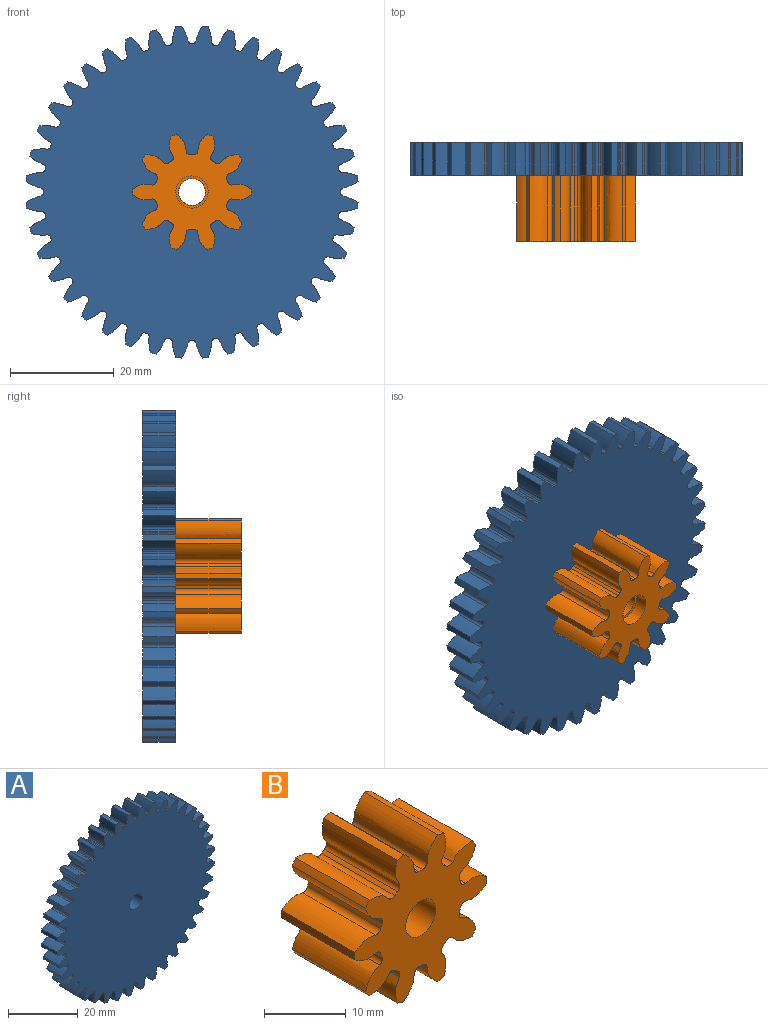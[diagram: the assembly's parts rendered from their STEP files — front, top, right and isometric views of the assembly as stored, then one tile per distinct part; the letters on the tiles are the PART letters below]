
ASSEMBLY  parts=2 mates=1
PART A: 245 faces, bbox 63.9x6.4x63.9 mm
  f0: cylinder r=2.59mm len=5.18mm, axis (0,-1,0), area 62.7mm2, adj f40,f243
  f1: cylinder r=32mm len=6.35mm, axis (0,1,0), area 7.4mm2, adj f40,f42,f148,f240
  f2: cylinder r=32mm len=6.35mm, axis (0,1,0), area 7.4mm2, adj f40,f42,f235,f238
  f3: cylinder r=32mm len=6.35mm, axis (0,1,0), area 7.4mm2, adj f40,f42,f230,f233
  f4: cylinder r=32mm len=6.35mm, axis (0,1,0), area 7.4mm2, adj f40,f42,f225,f228
  f5: cylinder r=32mm len=6.35mm, axis (0,1,0), area 7.4mm2, adj f40,f42,f220,f223
  f6: cylinder r=32mm len=6.35mm, axis (0,1,0), area 7.4mm2, adj f40,f42,f215,f218
  f7: cylinder r=32mm len=6.35mm, axis (0,1,0), area 7.4mm2, adj f40,f42,f210,f213
  f8: cylinder r=32mm len=6.35mm, axis (0,1,0), area 7.4mm2, adj f40,f42,f205,f208
  f9: cylinder r=32mm len=6.35mm, axis (0,1,0), area 7.4mm2, adj f40,f42,f193,f200
  f10: cylinder r=32mm len=6.35mm, axis (0,1,0), area 7.4mm2, adj f40,f42,f195,f203
  f11: cylinder r=32mm len=6.35mm, axis (0,1,0), area 7.4mm2, adj f40,f42,f190,f198
  f12: cylinder r=32mm len=6.35mm, axis (0,1,0), area 7.4mm2, adj f40,f42,f185,f188
  f13: cylinder r=32mm len=6.35mm, axis (0,1,0), area 7.4mm2, adj f40,f42,f180,f183
  f14: cylinder r=32mm len=6.35mm, axis (0,1,0), area 7.4mm2, adj f40,f42,f175,f178
  f15: cylinder r=32mm len=6.35mm, axis (0,1,0), area 7.4mm2, adj f40,f42,f170,f173
  f16: cylinder r=32mm len=6.35mm, axis (0,1,0), area 7.4mm2, adj f40,f42,f165,f168
  f17: cylinder r=32mm len=6.35mm, axis (0,1,0), area 7.4mm2, adj f40,f42,f138,f160
  f18: cylinder r=32mm len=6.35mm, axis (0,1,0), area 7.4mm2, adj f40,f42,f155,f158
  f19: cylinder r=32mm len=6.35mm, axis (0,1,0), area 7.4mm2, adj f40,f42,f143,f150
  f20: cylinder r=32mm len=6.35mm, axis (0,1,0), area 7.4mm2, adj f40,f42,f145,f153
  f21: cylinder r=32mm len=6.35mm, axis (0,1,0), area 7.4mm2, adj f40,f42,f133,f140
  f22: cylinder r=32mm len=6.35mm, axis (0,1,0), area 7.4mm2, adj f40,f42,f128,f135
  f23: cylinder r=32mm len=6.35mm, axis (0,1,0), area 7.4mm2, adj f40,f42,f123,f130
  f24: cylinder r=32mm len=6.35mm, axis (0,1,0), area 7.4mm2, adj f40,f42,f83,f125
  f25: cylinder r=32mm len=6.35mm, axis (0,1,0), area 7.4mm2, adj f40,f42,f43,f120
  f26: cylinder r=32mm len=6.35mm, axis (0,1,0), area 7.4mm2, adj f40,f42,f115,f118
  f27: cylinder r=32mm len=6.35mm, axis (0,1,0), area 7.4mm2, adj f40,f42,f110,f113
  f28: cylinder r=32mm len=6.35mm, axis (0,1,0), area 7.4mm2, adj f40,f42,f105,f108
  f29: cylinder r=32mm len=6.35mm, axis (0,1,0), area 7.4mm2, adj f40,f42,f93,f100
  f30: cylinder r=32mm len=6.35mm, axis (0,1,0), area 7.4mm2, adj f40,f42,f95,f103
  f31: cylinder r=32mm len=6.35mm, axis (0,1,0), area 7.4mm2, adj f40,f42,f90,f98
  f32: cylinder r=32mm len=6.35mm, axis (0,1,0), area 7.4mm2, adj f40,f42,f85,f88
  f33: cylinder r=32mm len=6.35mm, axis (0,1,0), area 7.4mm2, adj f40,f42,f68,f80
  f34: cylinder r=32mm len=6.35mm, axis (0,1,0), area 7.4mm2, adj f40,f42,f75,f78
  f35: cylinder r=32mm len=6.35mm, axis (0,1,0), area 7.4mm2, adj f40,f42,f63,f70
  f36: cylinder r=32mm len=6.35mm, axis (0,1,0), area 7.4mm2, adj f40,f42,f65,f163
  f37: cylinder r=32mm len=6.35mm, axis (0,1,0), area 7.4mm2, adj f40,f42,f60,f73
  f38: cylinder r=32mm len=6.35mm, axis (0,1,0), area 7.4mm2, adj f40,f42,f55,f58
  f39: cylinder r=32mm len=6.35mm, axis (0,1,0), area 7.4mm2, adj f40,f42,f50,f53
  f40: plane 63.89x63.89mm, normal (0,-1,0), area 2875.7mm2, adj f0,f1,f2,f3,f4,f5,f6,f7
  f41: cylinder r=32mm len=6.35mm, axis (0,1,0), area 7.4mm2, adj f40,f42,f45,f48
  f42: plane 63.89x63.89mm, normal (0,1,0), area 2866.6mm2, adj f1,f2,f3,f4,f5,f6,f7,f8
  f43: extruded ~6.35x2.93mm, area 20.2mm2, adj f25,f40,f42,f46
  f44: cylinder r=28.57mm len=6.35mm, axis (0,1,0), area 2.7mm2, adj f40,f42,f46,f47
  f45: extruded ~6.35x2.93mm, area 20.2mm2, adj f40,f41,f42,f47
  f46: cylinder r=0.54mm len=6.35mm, axis (0,1,0), area 4.8mm2, adj f40,f42,f43,f44
  f47: cylinder r=0.54mm len=6.35mm, axis (0,1,0), area 4.8mm2, adj f40,f42,f44,f45
  f48: extruded ~6.35x3.08mm, area 20.2mm2, adj f40,f41,f42,f51
  f49: cylinder r=28.57mm len=6.35mm, axis (0,1,0), area 2.7mm2, adj f40,f42,f51,f52
  f50: extruded ~6.35x2.71mm, area 20.2mm2, adj f39,f40,f42,f52
  f51: cylinder r=0.54mm len=6.35mm, axis (0,1,0), area 4.8mm2, adj f40,f42,f48,f49
  f52: cylinder r=0.54mm len=6.35mm, axis (0,1,0), area 4.8mm2, adj f40,f42,f49,f50
  f53: extruded ~6.35x3.16mm, area 20.2mm2, adj f39,f40,f42,f56
  f54: cylinder r=28.57mm len=6.35mm, axis (0,1,0), area 2.7mm2, adj f40,f42,f56,f57
  f55: extruded ~6.35x2.42mm, area 20.2mm2, adj f38,f40,f42,f57
  f56: cylinder r=0.54mm len=6.35mm, axis (0,1,0), area 4.8mm2, adj f40,f42,f53,f54
  f57: cylinder r=0.54mm len=6.35mm, axis (0,1,0), area 4.8mm2, adj f40,f42,f54,f55
  f58: extruded ~6.35x3.15mm, area 20.2mm2, adj f38,f40,f42,f61
  f59: cylinder r=28.57mm len=6.35mm, axis (0,1,0), area 2.7mm2, adj f40,f42,f61,f62
  f60: extruded ~6.35x2.39mm, area 20.2mm2, adj f37,f40,f42,f62
  f61: cylinder r=0.54mm len=6.35mm, axis (0,1,0), area 4.8mm2, adj f40,f42,f58,f59
  f62: cylinder r=0.54mm len=6.35mm, axis (0,1,0), area 4.8mm2, adj f40,f42,f59,f60
  f63: extruded ~6.35x2.39mm, area 20.2mm2, adj f35,f40,f42,f66
  f64: cylinder r=28.57mm len=6.35mm, axis (0,1,0), area 2.7mm2, adj f40,f42,f66,f67
  f65: extruded ~6.35x3.15mm, area 20.2mm2, adj f36,f40,f42,f67
  f66: cylinder r=0.54mm len=6.35mm, axis (0,1,0), area 4.8mm2, adj f40,f42,f63,f64
  f67: cylinder r=0.54mm len=6.35mm, axis (0,1,0), area 4.8mm2, adj f40,f42,f64,f65
  f68: extruded ~6.35x2.68mm, area 20.2mm2, adj f33,f40,f42,f71
  f69: cylinder r=28.57mm len=6.35mm, axis (0,1,0), area 2.7mm2, adj f40,f42,f71,f72
  f70: extruded ~6.35x3.07mm, area 20.2mm2, adj f35,f40,f42,f72
  f71: cylinder r=0.54mm len=6.35mm, axis (0,1,0), area 4.8mm2, adj f40,f42,f68,f69
  f72: cylinder r=0.54mm len=6.35mm, axis (0,1,0), area 4.8mm2, adj f40,f42,f69,f70
  f73: extruded ~6.35x3.07mm, area 20.2mm2, adj f37,f40,f42,f76
  f74: cylinder r=28.57mm len=6.35mm, axis (0,1,0), area 2.7mm2, adj f40,f42,f76,f77
  f75: extruded ~6.35x2.68mm, area 20.2mm2, adj f34,f40,f42,f77
  f76: cylinder r=0.54mm len=6.35mm, axis (0,1,0), area 4.8mm2, adj f40,f42,f73,f74
  f77: cylinder r=0.54mm len=6.35mm, axis (0,1,0), area 4.8mm2, adj f40,f42,f74,f75
  f78: extruded ~6.35x2.91mm, area 20.2mm2, adj f34,f40,f42,f81
  f79: cylinder r=28.57mm len=6.35mm, axis (0,1,0), area 2.7mm2, adj f40,f42,f81,f82
  f80: extruded ~6.35x2.91mm, area 20.2mm2, adj f33,f40,f42,f82
  f81: cylinder r=0.54mm len=6.35mm, axis (0,1,0), area 4.8mm2, adj f40,f42,f78,f79
  f82: cylinder r=0.54mm len=6.35mm, axis (0,1,0), area 4.8mm2, adj f40,f42,f79,f80
  f83: extruded ~6.35x3.16mm, area 20.2mm2, adj f24,f40,f42,f86
  f84: cylinder r=28.57mm len=6.35mm, axis (0,1,0), area 2.7mm2, adj f40,f42,f86,f87
  f85: extruded ~6.35x2.42mm, area 20.2mm2, adj f32,f40,f42,f87
  f86: cylinder r=0.54mm len=6.35mm, axis (0,1,0), area 4.8mm2, adj f40,f42,f83,f84
  f87: cylinder r=0.54mm len=6.35mm, axis (0,1,0), area 4.8mm2, adj f40,f42,f84,f85
  f88: extruded ~6.35x3.15mm, area 20.2mm2, adj f32,f40,f42,f91
  f89: cylinder r=28.57mm len=6.35mm, axis (0,1,0), area 2.7mm2, adj f40,f42,f91,f92
  f90: extruded ~6.35x2.39mm, area 20.2mm2, adj f31,f40,f42,f92
  f91: cylinder r=0.54mm len=6.35mm, axis (0,1,0), area 4.8mm2, adj f40,f42,f88,f89
  f92: cylinder r=0.54mm len=6.35mm, axis (0,1,0), area 4.8mm2, adj f40,f42,f89,f90
  f93: extruded ~6.35x2.91mm, area 20.2mm2, adj f29,f40,f42,f96
  f94: cylinder r=28.57mm len=6.35mm, axis (0,1,0), area 2.7mm2, adj f40,f42,f96,f97
  f95: extruded ~6.35x2.91mm, area 20.2mm2, adj f30,f40,f42,f97
  f96: cylinder r=0.54mm len=6.35mm, axis (0,1,0), area 4.8mm2, adj f40,f42,f93,f94
  f97: cylinder r=0.54mm len=6.35mm, axis (0,1,0), area 4.8mm2, adj f40,f42,f94,f95
  f98: extruded ~6.35x3.07mm, area 20.2mm2, adj f31,f40,f42,f101
  f99: cylinder r=28.57mm len=6.35mm, axis (0,1,0), area 2.7mm2, adj f40,f42,f101,f102
  f100: extruded ~6.35x2.68mm, area 20.2mm2, adj f29,f40,f42,f102
  f101: cylinder r=0.54mm len=6.35mm, axis (0,1,0), area 4.8mm2, adj f40,f42,f98,f99
  f102: cylinder r=0.54mm len=6.35mm, axis (0,1,0), area 4.8mm2, adj f40,f42,f99,f100
  f103: extruded ~6.35x2.68mm, area 20.2mm2, adj f30,f40,f42,f106
  f104: cylinder r=28.57mm len=6.35mm, axis (0,1,0), area 2.7mm2, adj f40,f42,f106,f107
  f105: extruded ~6.35x3.07mm, area 20.2mm2, adj f28,f40,f42,f107
  f106: cylinder r=0.54mm len=6.35mm, axis (0,1,0), area 4.8mm2, adj f40,f42,f103,f104
  f107: cylinder r=0.54mm len=6.35mm, axis (0,1,0), area 4.8mm2, adj f40,f42,f104,f105
  f108: extruded ~6.35x2.39mm, area 20.2mm2, adj f28,f40,f42,f111
  f109: cylinder r=28.57mm len=6.35mm, axis (0,1,0), area 2.7mm2, adj f40,f42,f111,f112
  f110: extruded ~6.35x3.15mm, area 20.2mm2, adj f27,f40,f42,f112
  f111: cylinder r=0.54mm len=6.35mm, axis (0,1,0), area 4.8mm2, adj f40,f42,f108,f109
  f112: cylinder r=0.54mm len=6.35mm, axis (0,1,0), area 4.8mm2, adj f40,f42,f109,f110
  f113: extruded ~6.35x2.42mm, area 20.2mm2, adj f27,f40,f42,f116
  f114: cylinder r=28.57mm len=6.35mm, axis (0,1,0), area 2.7mm2, adj f40,f42,f116,f117
  f115: extruded ~6.35x3.16mm, area 20.2mm2, adj f26,f40,f42,f117
  f116: cylinder r=0.54mm len=6.35mm, axis (0,1,0), area 4.8mm2, adj f40,f42,f113,f114
  f117: cylinder r=0.54mm len=6.35mm, axis (0,1,0), area 4.8mm2, adj f40,f42,f114,f115
  f118: extruded ~6.35x2.71mm, area 20.2mm2, adj f26,f40,f42,f121
  f119: cylinder r=28.57mm len=6.35mm, axis (0,1,0), area 2.7mm2, adj f40,f42,f121,f122
  f120: extruded ~6.35x3.08mm, area 20.2mm2, adj f25,f40,f42,f122
  f121: cylinder r=0.54mm len=6.35mm, axis (0,1,0), area 4.8mm2, adj f40,f42,f118,f119
  f122: cylinder r=0.54mm len=6.35mm, axis (0,1,0), area 4.8mm2, adj f40,f42,f119,f120
  f123: extruded ~6.35x3.08mm, area 20.2mm2, adj f23,f40,f42,f126
  f124: cylinder r=28.57mm len=6.35mm, axis (0,1,0), area 2.7mm2, adj f40,f42,f126,f127
  f125: extruded ~6.35x2.71mm, area 20.2mm2, adj f24,f40,f42,f127
  f126: cylinder r=0.54mm len=6.35mm, axis (0,1,0), area 4.8mm2, adj f40,f42,f123,f124
  f127: cylinder r=0.54mm len=6.35mm, axis (0,1,0), area 4.8mm2, adj f40,f42,f124,f125
  f128: extruded ~6.35x2.93mm, area 20.2mm2, adj f22,f40,f42,f131
  f129: cylinder r=28.57mm len=6.35mm, axis (0,1,0), area 2.7mm2, adj f40,f42,f131,f132
  f130: extruded ~6.35x2.93mm, area 20.2mm2, adj f23,f40,f42,f132
  f131: cylinder r=0.54mm len=6.35mm, axis (0,1,0), area 4.8mm2, adj f40,f42,f128,f129
  f132: cylinder r=0.54mm len=6.35mm, axis (0,1,0), area 4.8mm2, adj f40,f42,f129,f130
  f133: extruded ~6.35x2.71mm, area 20.2mm2, adj f21,f40,f42,f136
  f134: cylinder r=28.57mm len=6.35mm, axis (0,1,0), area 2.7mm2, adj f40,f42,f136,f137
  f135: extruded ~6.35x3.08mm, area 20.2mm2, adj f22,f40,f42,f137
  f136: cylinder r=0.54mm len=6.35mm, axis (0,1,0), area 4.8mm2, adj f40,f42,f133,f134
  f137: cylinder r=0.54mm len=6.35mm, axis (0,1,0), area 4.8mm2, adj f40,f42,f134,f135
  f138: extruded ~6.35x2.42mm, area 20.2mm2, adj f17,f40,f42,f141
  f139: cylinder r=28.57mm len=6.35mm, axis (0,1,0), area 2.7mm2, adj f40,f42,f141,f142
  f140: extruded ~6.35x3.16mm, area 20.2mm2, adj f21,f40,f42,f142
  f141: cylinder r=0.54mm len=6.35mm, axis (0,1,0), area 4.8mm2, adj f40,f42,f138,f139
  f142: cylinder r=0.54mm len=6.35mm, axis (0,1,0), area 4.8mm2, adj f40,f42,f139,f140
  f143: extruded ~6.35x2.91mm, area 20.2mm2, adj f19,f40,f42,f146
  f144: cylinder r=28.57mm len=6.35mm, axis (0,1,0), area 2.7mm2, adj f40,f42,f146,f147
  f145: extruded ~6.35x2.91mm, area 20.2mm2, adj f20,f40,f42,f147
  f146: cylinder r=0.54mm len=6.35mm, axis (0,1,0), area 4.8mm2, adj f40,f42,f143,f144
  f147: cylinder r=0.54mm len=6.35mm, axis (0,1,0), area 4.8mm2, adj f40,f42,f144,f145
  f148: extruded ~6.35x3.07mm, area 20.2mm2, adj f1,f40,f42,f151
  f149: cylinder r=28.57mm len=6.35mm, axis (0,1,0), area 2.7mm2, adj f40,f42,f151,f152
  f150: extruded ~6.35x2.68mm, area 20.2mm2, adj f19,f40,f42,f152
  f151: cylinder r=0.54mm len=6.35mm, axis (0,1,0), area 4.8mm2, adj f40,f42,f148,f149
  f152: cylinder r=0.54mm len=6.35mm, axis (0,1,0), area 4.8mm2, adj f40,f42,f149,f150
  f153: extruded ~6.35x2.68mm, area 20.2mm2, adj f20,f40,f42,f156
  f154: cylinder r=28.57mm len=6.35mm, axis (0,1,0), area 2.7mm2, adj f40,f42,f156,f157
  f155: extruded ~6.35x3.07mm, area 20.2mm2, adj f18,f40,f42,f157
  f156: cylinder r=0.54mm len=6.35mm, axis (0,1,0), area 4.8mm2, adj f40,f42,f153,f154
  f157: cylinder r=0.54mm len=6.35mm, axis (0,1,0), area 4.8mm2, adj f40,f42,f154,f155
  f158: extruded ~6.35x2.39mm, area 20.2mm2, adj f18,f40,f42,f161
  f159: cylinder r=28.57mm len=6.35mm, axis (0,1,0), area 2.7mm2, adj f40,f42,f161,f162
  f160: extruded ~6.35x3.15mm, area 20.2mm2, adj f17,f40,f42,f162
  f161: cylinder r=0.54mm len=6.35mm, axis (0,1,0), area 4.8mm2, adj f40,f42,f158,f159
  f162: cylinder r=0.54mm len=6.35mm, axis (0,1,0), area 4.8mm2, adj f40,f42,f159,f160
  f163: extruded ~6.35x2.42mm, area 20.2mm2, adj f36,f40,f42,f166
  f164: cylinder r=28.57mm len=6.35mm, axis (0,1,0), area 2.7mm2, adj f40,f42,f166,f167
  f165: extruded ~6.35x3.16mm, area 20.2mm2, adj f16,f40,f42,f167
  f166: cylinder r=0.54mm len=6.35mm, axis (0,1,0), area 4.8mm2, adj f40,f42,f163,f164
  f167: cylinder r=0.54mm len=6.35mm, axis (0,1,0), area 4.8mm2, adj f40,f42,f164,f165
  f168: extruded ~6.35x2.71mm, area 20.2mm2, adj f16,f40,f42,f171
  f169: cylinder r=28.57mm len=6.35mm, axis (0,1,0), area 2.7mm2, adj f40,f42,f171,f172
  f170: extruded ~6.35x3.08mm, area 20.2mm2, adj f15,f40,f42,f172
  f171: cylinder r=0.54mm len=6.35mm, axis (0,1,0), area 4.8mm2, adj f40,f42,f168,f169
  f172: cylinder r=0.54mm len=6.35mm, axis (0,1,0), area 4.8mm2, adj f40,f42,f169,f170
  f173: extruded ~6.35x2.93mm, area 20.2mm2, adj f15,f40,f42,f176
  f174: cylinder r=28.57mm len=6.35mm, axis (0,1,0), area 2.7mm2, adj f40,f42,f176,f177
  f175: extruded ~6.35x2.93mm, area 20.2mm2, adj f14,f40,f42,f177
  f176: cylinder r=0.54mm len=6.35mm, axis (0,1,0), area 4.8mm2, adj f40,f42,f173,f174
  f177: cylinder r=0.54mm len=6.35mm, axis (0,1,0), area 4.8mm2, adj f40,f42,f174,f175
  f178: extruded ~6.35x3.08mm, area 20.2mm2, adj f14,f40,f42,f181
  f179: cylinder r=28.57mm len=6.35mm, axis (0,1,0), area 2.7mm2, adj f40,f42,f181,f182
  f180: extruded ~6.35x2.71mm, area 20.2mm2, adj f13,f40,f42,f182
  f181: cylinder r=0.54mm len=6.35mm, axis (0,1,0), area 4.8mm2, adj f40,f42,f178,f179
  f182: cylinder r=0.54mm len=6.35mm, axis (0,1,0), area 4.8mm2, adj f40,f42,f179,f180
  f183: extruded ~6.35x3.16mm, area 20.2mm2, adj f13,f40,f42,f186
  f184: cylinder r=28.57mm len=6.35mm, axis (0,1,0), area 2.7mm2, adj f40,f42,f186,f187
  f185: extruded ~6.35x2.42mm, area 20.2mm2, adj f12,f40,f42,f187
  f186: cylinder r=0.54mm len=6.35mm, axis (0,1,0), area 4.8mm2, adj f40,f42,f183,f184
  f187: cylinder r=0.54mm len=6.35mm, axis (0,1,0), area 4.8mm2, adj f40,f42,f184,f185
  f188: extruded ~6.35x3.15mm, area 20.2mm2, adj f12,f40,f42,f191
  f189: cylinder r=28.57mm len=6.35mm, axis (0,1,0), area 2.7mm2, adj f40,f42,f191,f192
  f190: extruded ~6.35x2.39mm, area 20.2mm2, adj f11,f40,f42,f192
  f191: cylinder r=0.54mm len=6.35mm, axis (0,1,0), area 4.8mm2, adj f40,f42,f188,f189
  f192: cylinder r=0.54mm len=6.35mm, axis (0,1,0), area 4.8mm2, adj f40,f42,f189,f190
  f193: extruded ~6.35x2.91mm, area 20.2mm2, adj f9,f40,f42,f196
  f194: cylinder r=28.57mm len=6.35mm, axis (0,1,0), area 2.7mm2, adj f40,f42,f196,f197
  f195: extruded ~6.35x2.91mm, area 20.2mm2, adj f10,f40,f42,f197
  f196: cylinder r=0.54mm len=6.35mm, axis (0,1,0), area 4.8mm2, adj f40,f42,f193,f194
  f197: cylinder r=0.54mm len=6.35mm, axis (0,1,0), area 4.8mm2, adj f40,f42,f194,f195
  f198: extruded ~6.35x3.07mm, area 20.2mm2, adj f11,f40,f42,f201
  f199: cylinder r=28.57mm len=6.35mm, axis (0,1,0), area 2.7mm2, adj f40,f42,f201,f202
  f200: extruded ~6.35x2.68mm, area 20.2mm2, adj f9,f40,f42,f202
  f201: cylinder r=0.54mm len=6.35mm, axis (0,1,0), area 4.8mm2, adj f40,f42,f198,f199
  f202: cylinder r=0.54mm len=6.35mm, axis (0,1,0), area 4.8mm2, adj f40,f42,f199,f200
  f203: extruded ~6.35x2.68mm, area 20.2mm2, adj f10,f40,f42,f206
  f204: cylinder r=28.57mm len=6.35mm, axis (0,1,0), area 2.7mm2, adj f40,f42,f206,f207
  f205: extruded ~6.35x3.07mm, area 20.2mm2, adj f8,f40,f42,f207
  f206: cylinder r=0.54mm len=6.35mm, axis (0,1,0), area 4.8mm2, adj f40,f42,f203,f204
  f207: cylinder r=0.54mm len=6.35mm, axis (0,1,0), area 4.8mm2, adj f40,f42,f204,f205
  f208: extruded ~6.35x2.39mm, area 20.2mm2, adj f8,f40,f42,f211
  f209: cylinder r=28.57mm len=6.35mm, axis (0,1,0), area 2.7mm2, adj f40,f42,f211,f212
  f210: extruded ~6.35x3.15mm, area 20.2mm2, adj f7,f40,f42,f212
  f211: cylinder r=0.54mm len=6.35mm, axis (0,1,0), area 4.8mm2, adj f40,f42,f208,f209
  f212: cylinder r=0.54mm len=6.35mm, axis (0,1,0), area 4.8mm2, adj f40,f42,f209,f210
  f213: extruded ~6.35x2.42mm, area 20.2mm2, adj f7,f40,f42,f216
  f214: cylinder r=28.57mm len=6.35mm, axis (0,1,0), area 2.7mm2, adj f40,f42,f216,f217
  f215: extruded ~6.35x3.16mm, area 20.2mm2, adj f6,f40,f42,f217
  f216: cylinder r=0.54mm len=6.35mm, axis (0,1,0), area 4.8mm2, adj f40,f42,f213,f214
  f217: cylinder r=0.54mm len=6.35mm, axis (0,1,0), area 4.8mm2, adj f40,f42,f214,f215
  f218: extruded ~6.35x2.71mm, area 20.2mm2, adj f6,f40,f42,f221
  f219: cylinder r=28.57mm len=6.35mm, axis (0,1,0), area 2.7mm2, adj f40,f42,f221,f222
  f220: extruded ~6.35x3.08mm, area 20.2mm2, adj f5,f40,f42,f222
  f221: cylinder r=0.54mm len=6.35mm, axis (0,1,0), area 4.8mm2, adj f40,f42,f218,f219
  f222: cylinder r=0.54mm len=6.35mm, axis (0,1,0), area 4.8mm2, adj f40,f42,f219,f220
  f223: extruded ~6.35x2.93mm, area 20.2mm2, adj f5,f40,f42,f226
  f224: cylinder r=28.57mm len=6.35mm, axis (0,1,0), area 2.7mm2, adj f40,f42,f226,f227
  f225: extruded ~6.35x2.93mm, area 20.2mm2, adj f4,f40,f42,f227
  f226: cylinder r=0.54mm len=6.35mm, axis (0,1,0), area 4.8mm2, adj f40,f42,f223,f224
  f227: cylinder r=0.54mm len=6.35mm, axis (0,1,0), area 4.8mm2, adj f40,f42,f224,f225
  f228: extruded ~6.35x3.08mm, area 20.2mm2, adj f4,f40,f42,f231
  f229: cylinder r=28.57mm len=6.35mm, axis (0,1,0), area 2.7mm2, adj f40,f42,f231,f232
  f230: extruded ~6.35x2.71mm, area 20.2mm2, adj f3,f40,f42,f232
  f231: cylinder r=0.54mm len=6.35mm, axis (0,1,0), area 4.8mm2, adj f40,f42,f228,f229
  f232: cylinder r=0.54mm len=6.35mm, axis (0,1,0), area 4.8mm2, adj f40,f42,f229,f230
  f233: extruded ~6.35x3.16mm, area 20.2mm2, adj f3,f40,f42,f236
  f234: cylinder r=28.57mm len=6.35mm, axis (0,1,0), area 2.7mm2, adj f40,f42,f236,f237
  f235: extruded ~6.35x2.42mm, area 20.2mm2, adj f2,f40,f42,f237
  f236: cylinder r=0.54mm len=6.35mm, axis (0,1,0), area 4.8mm2, adj f40,f42,f233,f234
  f237: cylinder r=0.54mm len=6.35mm, axis (0,1,0), area 4.8mm2, adj f40,f42,f234,f235
  f238: extruded ~6.35x3.15mm, area 20.2mm2, adj f2,f40,f42,f241
  f239: cylinder r=28.57mm len=6.35mm, axis (0,1,0), area 2.7mm2, adj f40,f42,f241,f242
  f240: extruded ~6.35x2.39mm, area 20.2mm2, adj f1,f40,f42,f242
  f241: cylinder r=0.54mm len=6.35mm, axis (0,1,0), area 4.8mm2, adj f40,f42,f238,f239
  f242: cylinder r=0.54mm len=6.35mm, axis (0,1,0), area 4.8mm2, adj f40,f42,f239,f240
  f243: plane 6.2x6.2mm, normal (0,1,0), area 9.1mm2, adj f0,f244
  f244: cylinder r=3.1mm len=6.2mm, axis (0,1,0), area 48.7mm2, adj f42,f243
PART B: 65 faces, bbox 22.9x12.7x22.1 mm
  f0: cylinder r=2.58mm len=10.2mm, axis (0,-1,0), area 165.6mm2, adj f10,f63
  f1: cylinder r=11.43mm len=12.7mm, axis (0,1,0), area 14.2mm2, adj f10,f12,f15,f59
  f2: cylinder r=11.43mm len=12.7mm, axis (0,1,0), area 14.2mm2, adj f10,f12,f54,f60
  f3: cylinder r=11.43mm len=12.7mm, axis (0,1,0), area 14.2mm2, adj f10,f12,f45,f49
  f4: cylinder r=11.43mm len=12.7mm, axis (0,1,0), area 14.2mm2, adj f10,f12,f44,f55
  f5: cylinder r=11.43mm len=12.7mm, axis (0,1,0), area 14.2mm2, adj f10,f12,f35,f39
  f6: cylinder r=11.43mm len=12.7mm, axis (0,1,0), area 14.2mm2, adj f10,f12,f34,f50
  f7: cylinder r=11.43mm len=12.7mm, axis (0,1,0), area 14.2mm2, adj f10,f12,f29,f40
  f8: cylinder r=11.43mm len=12.7mm, axis (0,1,0), area 14.2mm2, adj f10,f12,f24,f30
  f9: cylinder r=11.43mm len=12.7mm, axis (0,1,0), area 14.2mm2, adj f10,f12,f19,f25
  f10: plane 22.9x22.11mm, normal (0,-1,0), area 251.7mm2, adj f0,f1,f2,f3,f4,f5,f6,f7
  f11: cylinder r=11.43mm len=12.7mm, axis (0,1,0), area 14.2mm2, adj f10,f12,f14,f20
  f12: plane 22.9x22.11mm, normal (0,1,0), area 242.4mm2, adj f1,f2,f3,f4,f5,f6,f7,f8
  f13: cylinder r=7.14mm len=12.7mm, axis (0,1,0), area 7.8mm2, adj f10,f12,f16,f17
  f14: extruded ~12.7x3.64mm, area 49.1mm2, adj f10,f11,f12,f16
  f15: extruded ~12.7x2.78mm, area 49.1mm2, adj f1,f10,f12,f17
  f16: cylinder r=0.78mm len=12.7mm, axis (0,1,0), area 14.7mm2, adj f10,f12,f13,f14
  f17: cylinder r=0.78mm len=12.7mm, axis (0,1,0), area 14.7mm2, adj f10,f12,f13,f15
  f18: cylinder r=7.14mm len=12.7mm, axis (0,1,0), area 7.8mm2, adj f10,f12,f21,f22
  f19: extruded ~12.7x2.78mm, area 49.1mm2, adj f9,f10,f12,f21
  f20: extruded ~12.7x3.64mm, area 49.1mm2, adj f10,f11,f12,f22
  f21: cylinder r=0.78mm len=12.7mm, axis (0,1,0), area 14.7mm2, adj f10,f12,f18,f19
  f22: cylinder r=0.78mm len=12.7mm, axis (0,1,0), area 14.7mm2, adj f10,f12,f18,f20
  f23: cylinder r=7.14mm len=12.7mm, axis (0,1,0), area 7.8mm2, adj f10,f12,f26,f27
  f24: extruded ~12.7x3.71mm, area 49.1mm2, adj f8,f10,f12,f26
  f25: extruded ~12.7x3.41mm, area 49.1mm2, adj f9,f10,f12,f27
  f26: cylinder r=0.78mm len=12.7mm, axis (0,1,0), area 14.7mm2, adj f10,f12,f23,f24
  f27: cylinder r=0.78mm len=12.7mm, axis (0,1,0), area 14.7mm2, adj f10,f12,f23,f25
  f28: cylinder r=7.14mm len=12.7mm, axis (0,1,0), area 7.8mm2, adj f10,f12,f31,f32
  f29: extruded ~12.7x3.22mm, area 49.1mm2, adj f7,f10,f12,f31
  f30: extruded ~12.7x3.22mm, area 49.1mm2, adj f8,f10,f12,f32
  f31: cylinder r=0.78mm len=12.7mm, axis (0,1,0), area 14.7mm2, adj f10,f12,f28,f29
  f32: cylinder r=0.78mm len=12.7mm, axis (0,1,0), area 14.7mm2, adj f10,f12,f28,f30
  f33: cylinder r=7.14mm len=12.7mm, axis (0,1,0), area 7.8mm2, adj f10,f12,f36,f37
  f34: extruded ~12.7x3.64mm, area 49.1mm2, adj f6,f10,f12,f36
  f35: extruded ~12.7x2.78mm, area 49.1mm2, adj f5,f10,f12,f37
  f36: cylinder r=0.78mm len=12.7mm, axis (0,1,0), area 14.7mm2, adj f10,f12,f33,f34
  f37: cylinder r=0.78mm len=12.7mm, axis (0,1,0), area 14.7mm2, adj f10,f12,f33,f35
  f38: cylinder r=7.14mm len=12.7mm, axis (0,1,0), area 7.8mm2, adj f10,f12,f41,f42
  f39: extruded ~12.7x3.41mm, area 49.1mm2, adj f5,f10,f12,f41
  f40: extruded ~12.7x3.71mm, area 49.1mm2, adj f7,f10,f12,f42
  f41: cylinder r=0.78mm len=12.7mm, axis (0,1,0), area 14.7mm2, adj f10,f12,f38,f39
  f42: cylinder r=0.78mm len=12.7mm, axis (0,1,0), area 14.7mm2, adj f10,f12,f38,f40
  f43: cylinder r=7.14mm len=12.7mm, axis (0,1,0), area 7.8mm2, adj f10,f12,f46,f47
  f44: extruded ~12.7x3.71mm, area 49.1mm2, adj f4,f10,f12,f46
  f45: extruded ~12.7x3.41mm, area 49.1mm2, adj f3,f10,f12,f47
  f46: cylinder r=0.78mm len=12.7mm, axis (0,1,0), area 14.7mm2, adj f10,f12,f43,f44
  f47: cylinder r=0.78mm len=12.7mm, axis (0,1,0), area 14.7mm2, adj f10,f12,f43,f45
  f48: cylinder r=7.14mm len=12.7mm, axis (0,1,0), area 7.8mm2, adj f10,f12,f51,f52
  f49: extruded ~12.7x2.78mm, area 49.1mm2, adj f3,f10,f12,f51
  f50: extruded ~12.7x3.64mm, area 49.1mm2, adj f6,f10,f12,f52
  f51: cylinder r=0.78mm len=12.7mm, axis (0,1,0), area 14.7mm2, adj f10,f12,f48,f49
  f52: cylinder r=0.78mm len=12.7mm, axis (0,1,0), area 14.7mm2, adj f10,f12,f48,f50
  f53: cylinder r=7.14mm len=12.7mm, axis (0,1,0), area 7.8mm2, adj f10,f12,f56,f57
  f54: extruded ~12.7x3.22mm, area 49.1mm2, adj f2,f10,f12,f56
  f55: extruded ~12.7x3.22mm, area 49.1mm2, adj f4,f10,f12,f57
  f56: cylinder r=0.78mm len=12.7mm, axis (0,1,0), area 14.7mm2, adj f10,f12,f53,f54
  f57: cylinder r=0.78mm len=12.7mm, axis (0,1,0), area 14.7mm2, adj f10,f12,f53,f55
  f58: cylinder r=7.14mm len=12.7mm, axis (0,1,0), area 7.8mm2, adj f10,f12,f61,f62
  f59: extruded ~12.7x3.41mm, area 49.1mm2, adj f1,f10,f12,f61
  f60: extruded ~12.7x3.71mm, area 49.1mm2, adj f2,f10,f12,f62
  f61: cylinder r=0.78mm len=12.7mm, axis (0,1,0), area 14.7mm2, adj f10,f12,f58,f59
  f62: cylinder r=0.78mm len=12.7mm, axis (0,1,0), area 14.7mm2, adj f10,f12,f58,f60
  f63: plane 6.2x6.2mm, normal (0,1,0), area 9.2mm2, adj f0,f64
  f64: cylinder r=3.1mm len=6.2mm, axis (0,1,0), area 48.7mm2, adj f12,f63
PLACE A at identity fixed
PLACE B rot(axis=(0,0,1),180deg) t=(0,-19.05,0)mm
MATE fastened B.f0 <-> A.f1  axis (0,1,0) through (0,-6.35,0)mm
